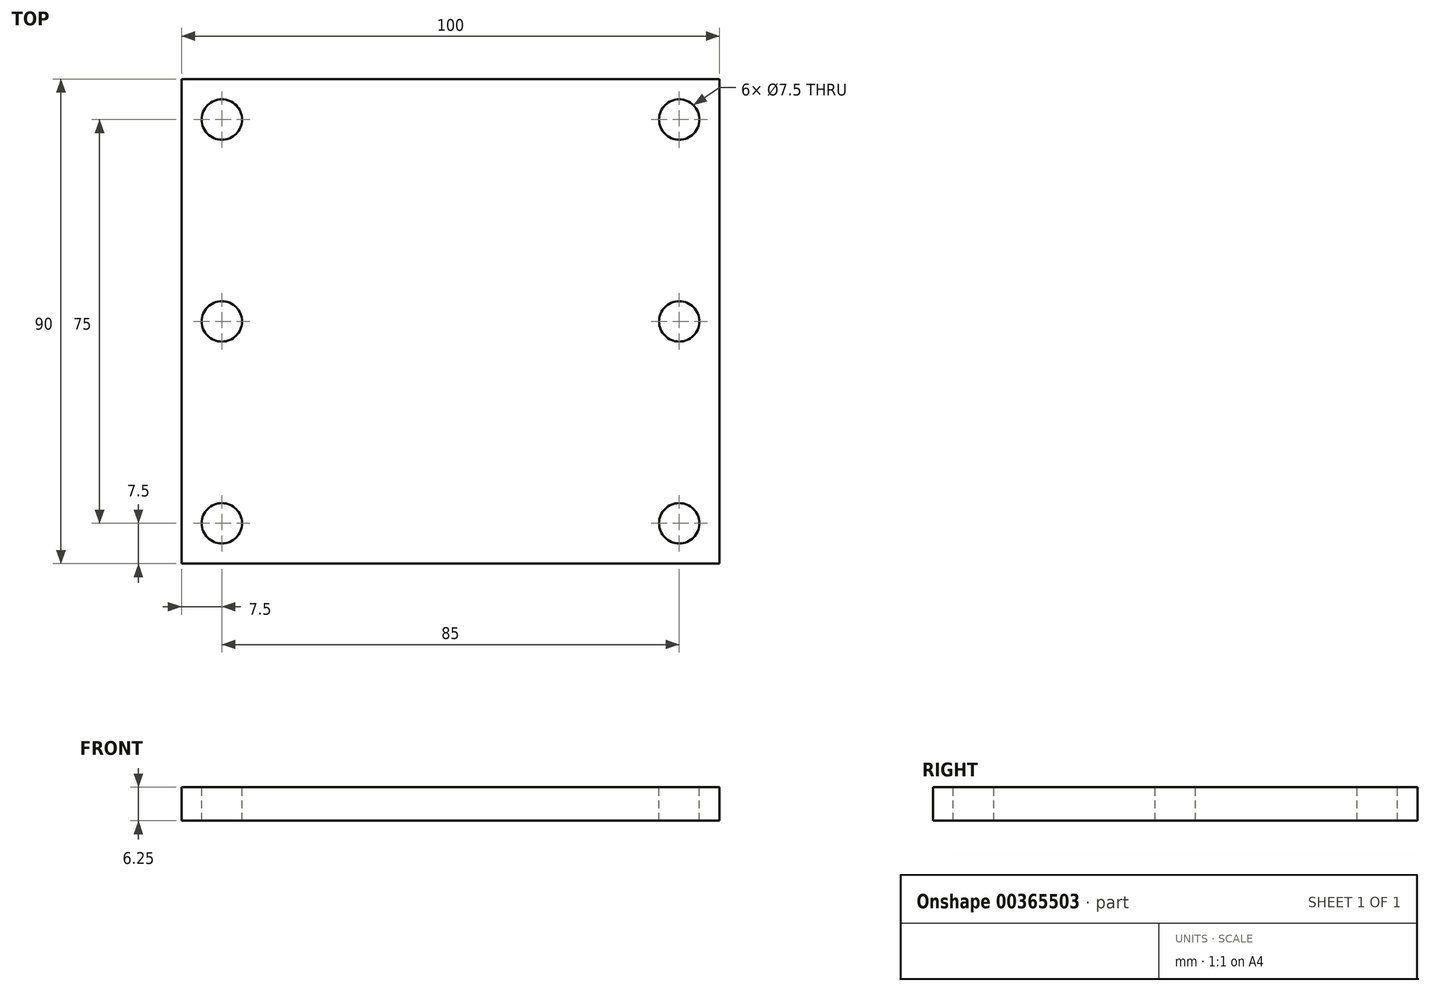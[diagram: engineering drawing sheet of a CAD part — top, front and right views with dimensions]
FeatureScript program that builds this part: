
annotation { "Feature Type Name" : "Feature", "Feature Type Description" : "" }
export const myFeature = defineFeature(function(context is Context, id is Id, definition is map)
    precondition{}
    {
        {
            var Q0;
            Q0=qCreatedBy(makeId("Top.planeOp"),FACE);
            var sketch = newSketch(context, id + "F0", { "sketchPlane" : qUnion([Q0])});
            skLineSegment(sketch, "E0.bottom", {"start": v(50, 45) * mm, "end": v(-50, 45) * mm});
            skLineSegment(sketch, "E0.top", {"start": v(50, -45) * mm, "end": v(-50, -45) * mm});
            skLineSegment(sketch, "E0.left", {"start": v(50, 45) * mm, "end": v(50, -45) * mm});
            skLineSegment(sketch, "E0.right", {"start": v(-50, 45) * mm, "end": v(-50, -45) * mm});
            skPoint(sketch, "E0.middle", {"position": v(0, 0) * mm});
            skSolve(sketch);
        }
        {
            var Q0;
            Q0 = qSketchRegion(id + "F0", true);
            extrude(context, id + "F1", {"entities" : qUnion([Q0]), "depth" : 6.25 * mm, "offsetDistance" : 25 * mm});
        }
        {
            var Q0;
            Q0=makeQuery(id+"F1.opExtrude","CAP_FACE",FACE,{"disambiguationData":[OSD([sQuery(id+"F0.wireOp",EDGE,"E0.bottom"),sQuery(id+"F0.wireOp",EDGE,"E0.top"),sQuery(id+"F0.wireOp",EDGE,"E0.left"),sQuery(id+"F0.wireOp",EDGE,"E0.right")])],"isStart":false});
            var sketch = newSketch(context, id + "F2", { "sketchPlane" : qUnion([Q0])});
            skCircle(sketch, "E1", {"center": v(-42.5, 37.5) * mm, "radius": 3.75 * mm});
            skCircle(sketch, "E2", {"center": v(-42.5, -37.5) * mm, "radius": 3.75 * mm});
            skCircle(sketch, "E3", {"center": v(-42.5, 0) * mm, "radius": 3.75 * mm});
            skCircle(sketch, "E4", {"center": v(42.5, 37.5) * mm, "radius": 3.75 * mm});
            skCircle(sketch, "E5", {"center": v(42.5, 0) * mm, "radius": 3.75 * mm});
            skCircle(sketch, "E6", {"center": v(42.5, -37.5) * mm, "radius": 3.75 * mm});
            skSolve(sketch);
        }
        {
            var Q0;
            Q0 = qSketchRegion(id + "F2", true);
            extrude(context, id + "F3", {"entities" : qUnion([Q0]), "operationType" : NewBodyOperationType.REMOVE, "oppositeDirection" : true, "depth" : 25 * mm});
        }
    });
